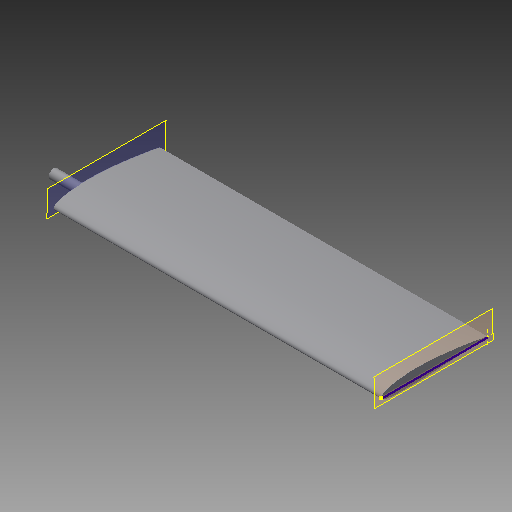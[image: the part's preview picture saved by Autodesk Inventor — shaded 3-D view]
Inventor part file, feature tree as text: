
AUTODESK INVENTOR PART (.ipt)
format: ipt  version: 2018 (Build 220112000, 112)  size: 111,616 bytes
history: native  units: in
note: dims shown in document units (in); Inventor stores cm internally (conversion verified against a paired STEP export)
features: sketch x3, plane x3, extrude x2, mirror x1
ambient origin geometry x8: Origin, YZ Plane, XZ Plane, XY Plane, X Axis, Y Axis, Z Axis, Center Point
bodies: Solid1 (feature_tree)
feature tree (9):
  extrude  "Extrusion1"  [1 undecoded]
  sketch  "Sketch2"  dims[d3=1.0in d4=2.9134in d5=0.0in]
  plane  "Work Plane1"
  plane  "Work Plane2"
  mirror  "Mirror1"
  extrude  "Extrusion2"  Depth=2.9134in TaperAngle=0.0deg
  sketch  "Sketch1"  dims[d0=33.8583in d1=0.0in d2=-0.0137in]
  plane  "Work Plane3"
  sketch  "Sketch3"
note: 1 required parameter value undecoded (feature->parameter linkage not recoverable at this tier; creation-order binding heuristic only, values carry confidence <= 0.55)
